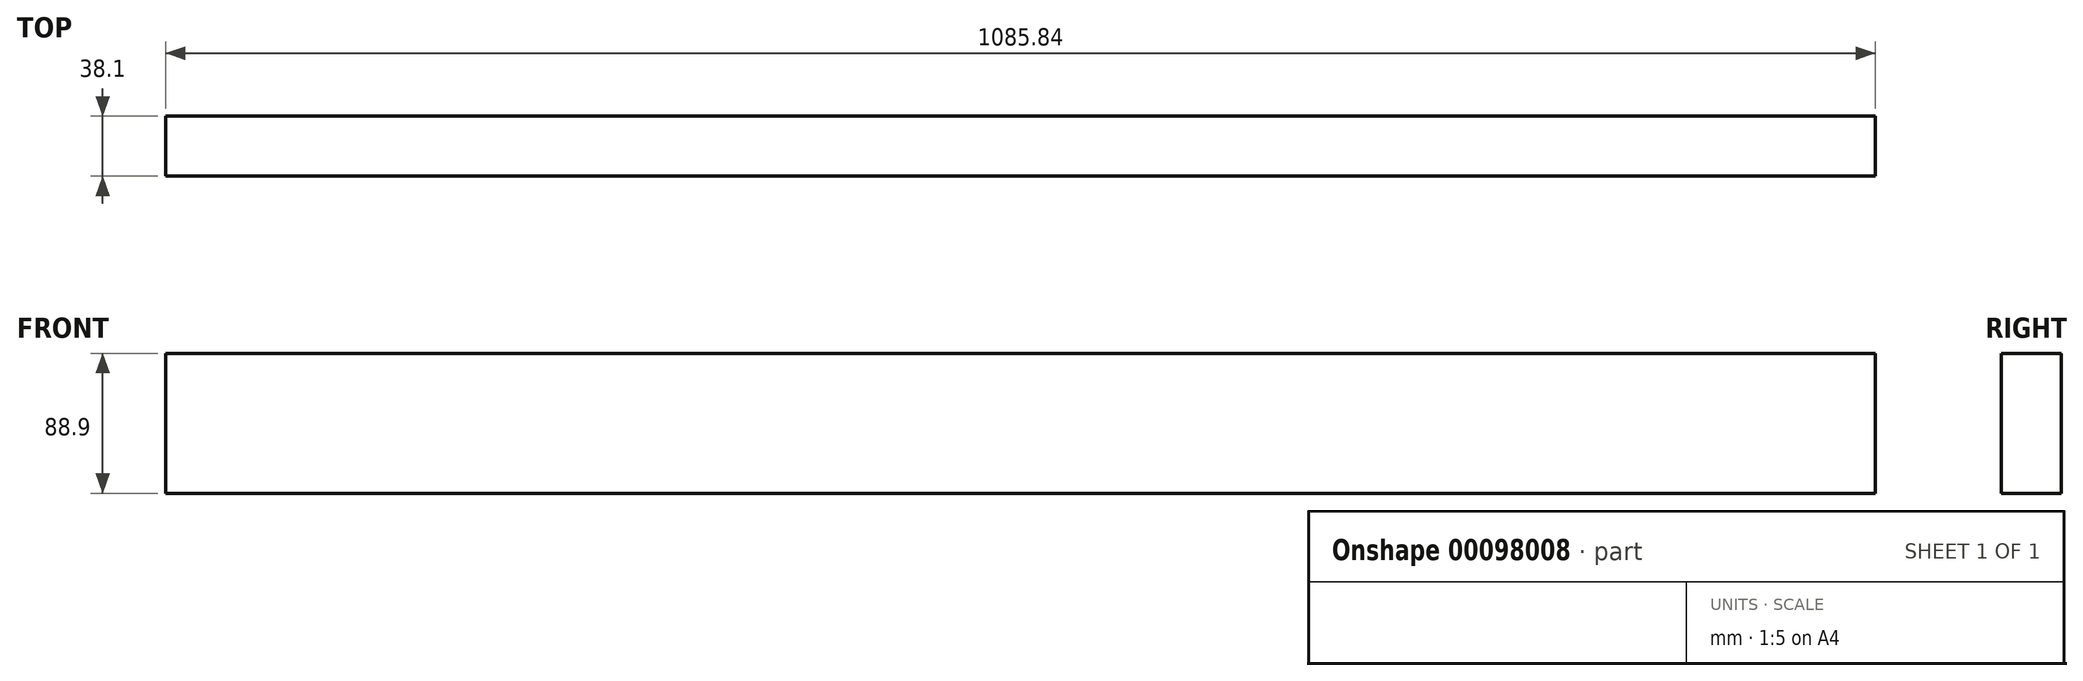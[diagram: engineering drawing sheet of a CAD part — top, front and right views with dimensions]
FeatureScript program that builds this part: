
annotation { "Feature Type Name" : "Feature", "Feature Type Description" : "" }
export const myFeature = defineFeature(function(context is Context, id is Id, definition is map)
    precondition{}
    {
        {
            var Q0;
            Q0=qCreatedBy(makeId("Front.planeOp"),FACE);
            var sketch = newSketch(context, id + "F0", { "sketchPlane" : qUnion([Q0])});
            skLineSegment(sketch, "E0.bottom", {"start": v(542.93, 44.45) * mm, "end": v(-542.93, 44.45) * mm});
            skLineSegment(sketch, "E0.top", {"start": v(542.93, -44.45) * mm, "end": v(-542.93, -44.45) * mm});
            skLineSegment(sketch, "E0.left", {"start": v(542.93, 44.45) * mm, "end": v(542.93, -44.45) * mm});
            skLineSegment(sketch, "E0.right", {"start": v(-542.93, 44.45) * mm, "end": v(-542.93, -44.45) * mm});
            skPoint(sketch, "E0.middle", {"position": v(0, 0) * mm});
            skSolve(sketch);
        }
        {
            var Q0;
            Q0=makeQuery(id+"F0.imprint","IMPRINT",FACE,{"disambiguationData":[TD([[makeQuery(id+"F0.imprint","IMPRINT",EDGE,{"derivedFrom":sQuery(id+"F0.wireOp",EDGE,"E0.bottom")}),1.0]])]});
            extrude(context, id + "F1", {"entities" : qUnion([Q0]), "depth" : 38.1 * mm});
        }
    });
